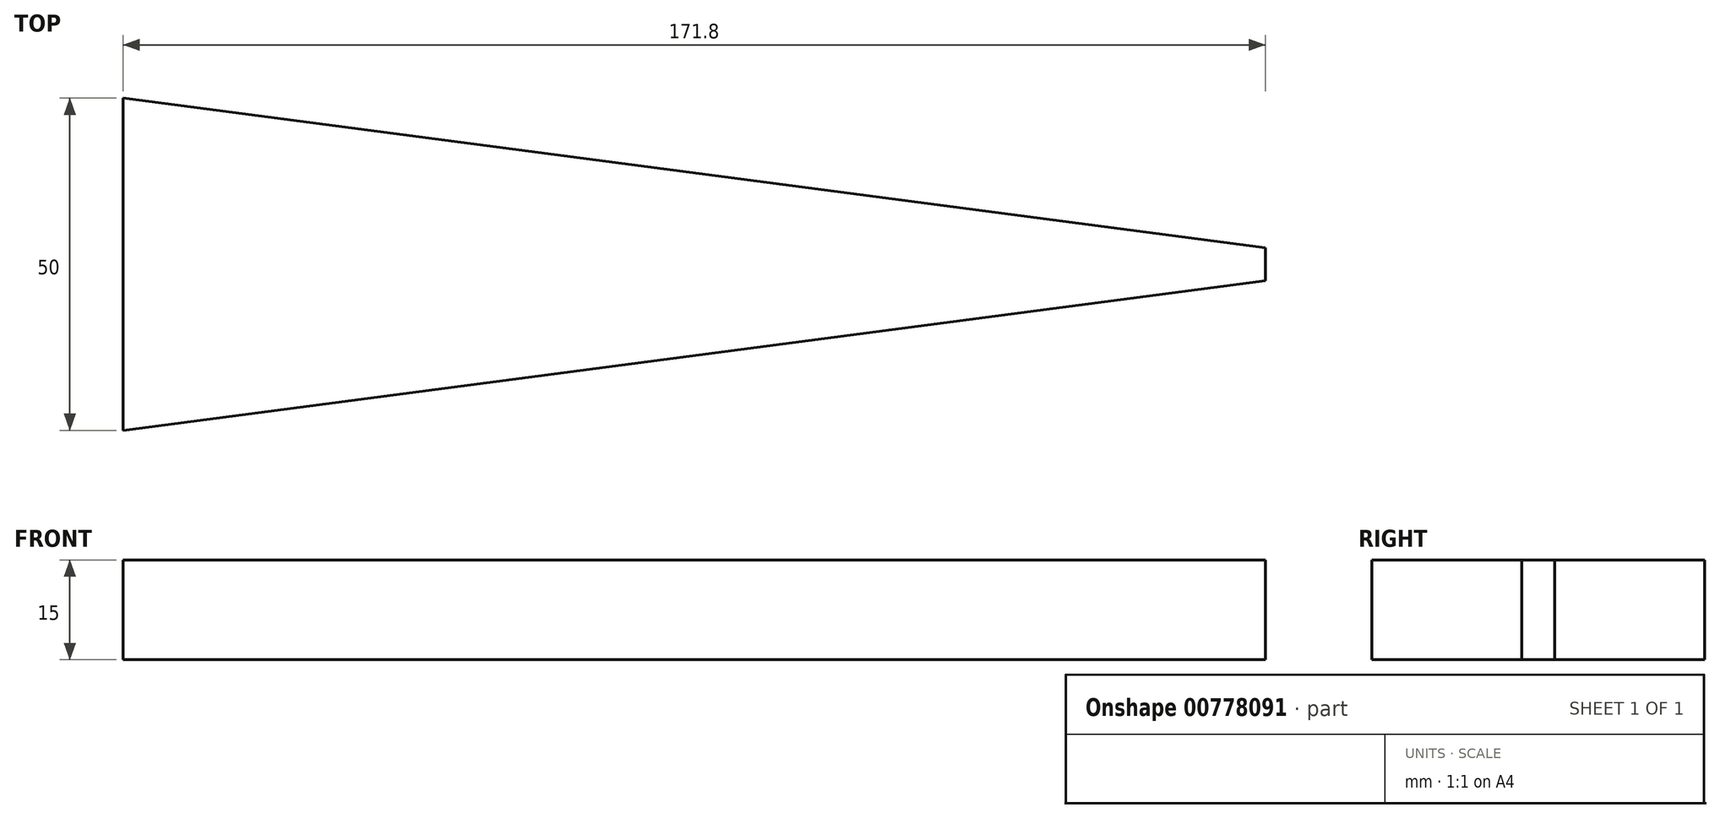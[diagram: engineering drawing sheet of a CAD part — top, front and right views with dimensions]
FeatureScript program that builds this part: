
annotation { "Feature Type Name" : "Feature", "Feature Type Description" : "" }
export const myFeature = defineFeature(function(context is Context, id is Id, definition is map)
    precondition{}
    {
        {
            var Q0;
            Q0=qCreatedBy(makeId("Top.planeOp"),FACE);
            var sketch = newSketch(context, id + "F0", { "sketchPlane" : qUnion([Q0])});
            skLineSegment(sketch, "E0", {"start": v(-85.9, -25) * mm, "end": v(85.9, -2.5) * mm});
            skLineSegment(sketch, "E1", {"start": v(85.9, -2.5) * mm, "end": v(85.9, 2.5) * mm});
            skLineSegment(sketch, "E2", {"start": v(85.9, 2.5) * mm, "end": v(-85.9, 25) * mm});
            skLineSegment(sketch, "E3", {"start": v(-85.9, 25) * mm, "end": v(-85.9, -25) * mm});
            skLineSegment(sketch, "E4", {"start": v(0, 13.75) * mm, "end": v(0, -13.75) * mm, "construction": true});
            skLineSegment(sketch, "E5", {"start": v(-85.9, 0) * mm, "end": v(85.9, 0) * mm, "construction": true});
            skPoint(sketch, "E5.startSnap0", {"position": v(-85.9, 0) * mm});
            skSolve(sketch);
        }
        {
            var Q0;
            Q0=makeQuery(id+"F0.imprint","IMPRINT",FACE,{"disambiguationData":[TD([[makeQuery(id+"F0.imprint","IMPRINT",EDGE,{"derivedFrom":sQuery(id+"F0.wireOp",EDGE,"E0")}),1.0]])]});
            extrude(context, id + "F1", {"entities" : qUnion([Q0]), "depth" : 15 * mm, "offsetDistance" : 25 * mm});
        }
    });
